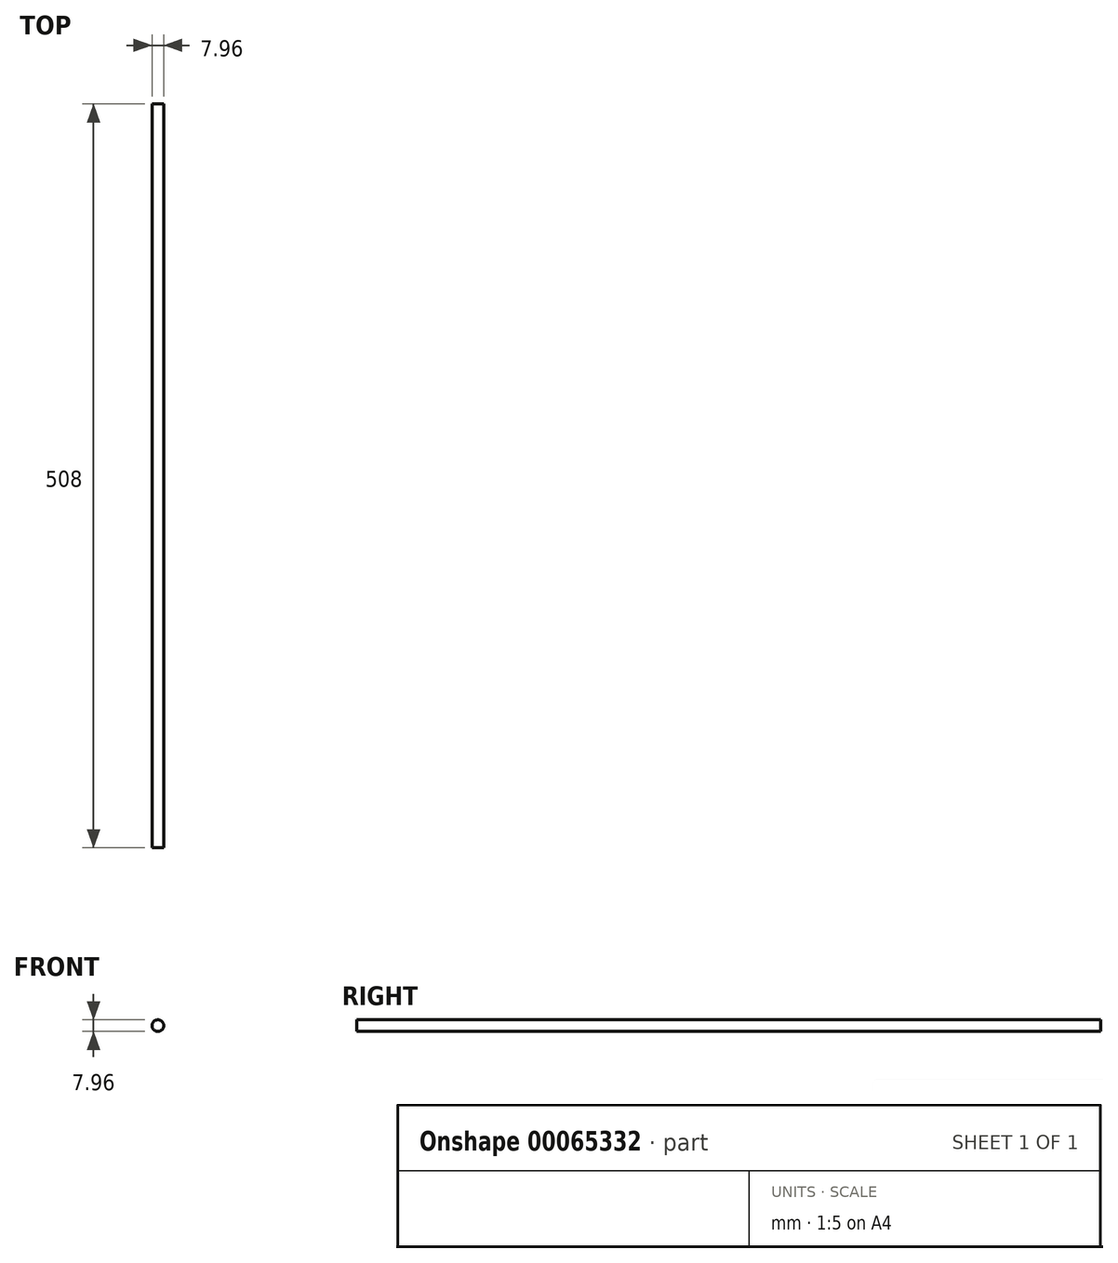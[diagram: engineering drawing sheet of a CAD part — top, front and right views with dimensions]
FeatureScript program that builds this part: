
annotation { "Feature Type Name" : "Feature", "Feature Type Description" : "" }
export const myFeature = defineFeature(function(context is Context, id is Id, definition is map)
    precondition{}
    {
        {
            var Q0;
            Q0=qCreatedBy(makeId("Front.planeOp"),FACE);
            var sketch = newSketch(context, id + "F0", { "sketchPlane" : qUnion([Q0])});
            skCircle(sketch, "E0", {"center": v(0, 0) * mm, "radius": 3.98 * mm});
            skSolve(sketch);
        }
        {
            var Q0;
            Q0=makeQuery(id+"F0.imprint","IMPRINT",FACE,{"disambiguationData":[TD([[makeQuery(id+"F0.imprint","IMPRINT",EDGE,{"derivedFrom":sQuery(id+"F0.wireOp",EDGE,"E0")}),1.0]])]});
            extrude(context, id + "F1", {"entities" : qUnion([Q0]), "depth" : 508 * mm});
        }
    });
